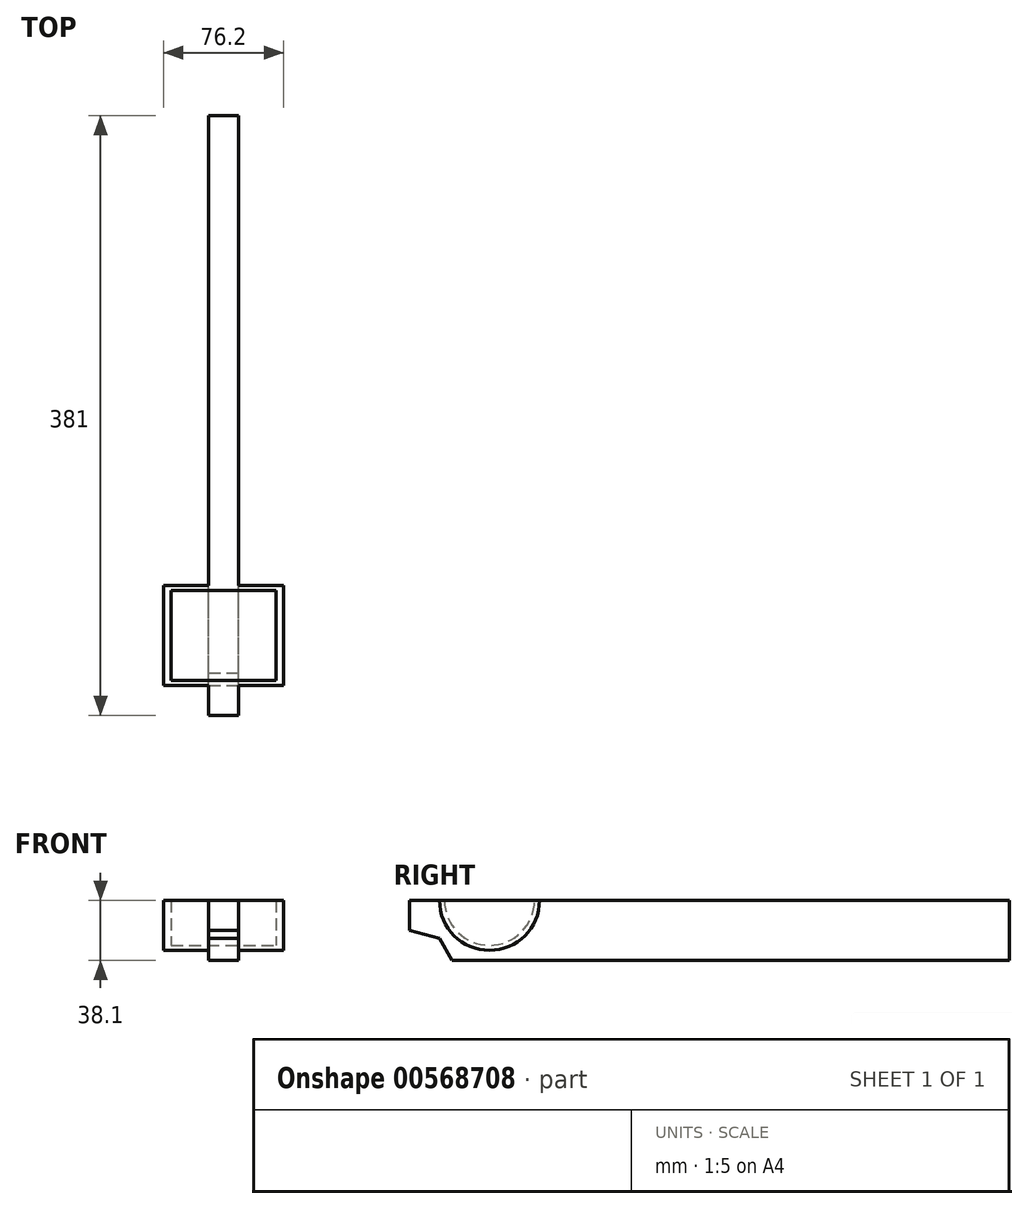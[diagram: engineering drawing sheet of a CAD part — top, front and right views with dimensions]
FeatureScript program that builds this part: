
annotation { "Feature Type Name" : "Feature", "Feature Type Description" : "" }
export const myFeature = defineFeature(function(context is Context, id is Id, definition is map)
    precondition{}
    {
        {
            var Q0;
            Q0=qCreatedBy(makeId("Front.planeOp"),FACE);
            var sketch = newSketch(context, id + "F0", { "sketchPlane" : qUnion([Q0])});
            skLineSegment(sketch, "E0.bottom", {"start": v(9.52, 19.05) * mm, "end": v(-9.53, 19.05) * mm});
            skLineSegment(sketch, "E0.top", {"start": v(9.52, -19.05) * mm, "end": v(-9.52, -19.05) * mm});
            skLineSegment(sketch, "E0.left", {"start": v(9.53, 19.05) * mm, "end": v(9.52, -19.05) * mm});
            skLineSegment(sketch, "E0.right", {"start": v(-9.53, 19.05) * mm, "end": v(-9.53, -19.05) * mm});
            skPoint(sketch, "E0.middle", {"position": v(0, 0) * mm});
            skSolve(sketch);
        }
        {
            var Q0;
            Q0 = qSketchRegion(id + "F0", true);
            extrude(context, id + "F1", {"entities" : qUnion([Q0]), "endBound" : BoundingType.SYMMETRIC, "depth" : 381 * mm, "offsetDistance" : 25.4 * mm});
        }
        {
            var Q0;
            Q0=qCreatedBy(makeId("Right.planeOp"),FACE);
            var sketch = newSketch(context, id + "F2", { "sketchPlane" : qUnion([Q0])});
            skLineSegment(sketch, "E1.1", {"start": v(-190.5, 19.05) * mm, "end": v(-190.5, -19.05) * mm, "construction": true});
            skLineSegment(sketch, "E1.2", {"start": v(-190.5, -19.05) * mm, "end": v(190.5, -19.05) * mm, "construction": true});
            skArc(sketch, "E2", {"start": v(-171.45, 19.05) * mm, "mid": v(-139.7, -12.7) * mm, "end": v(-107.95, 19.05) * mm});
            skLineSegment(sketch, "E3.0", {"start": v(-171.45, 19.05) * mm, "end": v(-107.95, 19.05) * mm});
            skPoint(sketch, "E4.orphan", {"position": v(190.5, 19.05) * mm});
            skSolve(sketch);
        }
        {
            var Q0;
            Q0 = qSketchRegion(id + "F2", true);
            extrude(context, id + "F3", {"entities" : qUnion([Q0]), "operationType" : NewBodyOperationType.ADD, "endBound" : BoundingType.SYMMETRIC, "depth" : 76.2 * mm, "offsetDistance" : 25.4 * mm});
        }
        {
            var Q0;
            Q0=makeQuery(id+"F3.boolean.opBoolean","MERGE",FACE,{"derivedFrom":[makeQuery(id+"F1.opExtrude","SWEPT_FACE",FACE,{"disambiguationData":[OSD([sQuery(id+"F0.wireOp",EDGE,"E0.bottom")])]}),makeQuery(id+"F3.opExtrude","SWEPT_FACE",FACE,{"disambiguationData":[OSD([sQuery(id+"F2.wireOp",EDGE,"E3.0")])]})]});
            var sketch = newSketch(context, id + "F4", { "sketchPlane" : qUnion([Q0])});
            skLineSegment(sketch, "E5", {"start": v(-9.52, -107.95) * mm, "end": v(9.53, -107.95) * mm, "construction": true});
            skLineSegment(sketch, "E6.1", {"start": v(-38.1, -171.45) * mm, "end": v(-38.1, -107.95) * mm, "construction": true});
            skLineSegment(sketch, "E6.2", {"start": v(-9.52, -107.95) * mm, "end": v(-38.1, -107.95) * mm, "construction": true});
            skLineSegment(sketch, "E6.3", {"start": v(38.1, -107.95) * mm, "end": v(9.53, -107.95) * mm, "construction": true});
            skLineSegment(sketch, "E6.4", {"start": v(38.1, -171.45) * mm, "end": v(38.1, -107.95) * mm, "construction": true});
            skLineSegment(sketch, "E7", {"start": v(-33.34, -168.28) * mm, "end": v(-33.34, -111.13) * mm});
            skLineSegment(sketch, "E8", {"start": v(-33.34, -111.13) * mm, "end": v(33.34, -111.13) * mm});
            skLineSegment(sketch, "E9", {"start": v(33.34, -111.12) * mm, "end": v(33.34, -168.28) * mm});
            skLineSegment(sketch, "E10", {"start": v(33.34, -168.28) * mm, "end": v(-33.34, -168.28) * mm});
            skLineSegment(sketch, "E11", {"start": v(-38.1, -171.45) * mm, "end": v(38.1, -171.45) * mm, "construction": true});
            skSolve(sketch);
        }
        {
            var Q0;
            Q0=makeQuery(id+"F3.opExtrude","CAP_FACE",FACE,{"disambiguationData":[OSD([sQuery(id+"F2.wireOp",EDGE,"E2"),sQuery(id+"F2.wireOp",EDGE,"E3.0")])],"isStart":false});
            var sketch = newSketch(context, id + "F5", { "sketchPlane" : qUnion([Q0])});
            skArc(sketch, "E12.0", {"start": v(-171.45, 19.05) * mm, "mid": v(-139.7, -12.7) * mm, "end": v(-107.95, 19.05) * mm, "construction": true});
            skLineSegment(sketch, "E13", {"start": v(-166.69, 19.05) * mm, "end": v(-112.71, 19.05) * mm});
            skArc(sketch, "E14.0", {"start": v(-166.69, 19.05) * mm, "mid": v(-139.7, -7.94) * mm, "end": v(-112.71, 19.05) * mm});
            skSolve(sketch);
        }
        {
            var Q0;
            Q0=makeQuery(id+"F4.imprint","IMPRINT",FACE,{"disambiguationData":[TD([[makeQuery(id+"F4.imprint","IMPRINT",EDGE,{"derivedFrom":sQuery(id+"F4.wireOp",EDGE,"E7")}),-1.0]])]});
            var sketch = newSketch(context, id + "F6", { "sketchPlane" : qUnion([Q0])});
            skLineSegment(sketch, "E15", {"start": v(38.1, -139.7) * mm, "end": v(78.66, -139.7) * mm, "construction": true});
            skLineSegment(sketch, "E16.bottom", {"start": v(33.34, -111.12) * mm, "end": v(-33.34, -111.12) * mm});
            skLineSegment(sketch, "E16.top", {"start": v(33.34, -139.7) * mm, "end": v(-33.34, -139.7) * mm});
            skLineSegment(sketch, "E16.left", {"start": v(33.34, -111.12) * mm, "end": v(33.34, -139.7) * mm});
            skLineSegment(sketch, "E16.right", {"start": v(-33.34, -111.13) * mm, "end": v(-33.34, -139.7) * mm});
            skSolve(sketch);
        }
        {
            var Q0;
            Q0 = qSketchRegion(id + "F6", true);
            var Q1;
            Q1=sQuery(id+"F6.wireOp",EDGE,"E15");
            revolve(context, id + "F7", {"operationType" : NewBodyOperationType.REMOVE, "entities" : qUnion([Q0]), "axis" : qUnion([Q1]), "revolveType" : RevolveType.FULL, "oppositeDirection" : true});
        }
        {
            var Q0;
            Q0=makeQuery(id+"F1.opExtrude","SWEPT_FACE",FACE,{"disambiguationData":[OSD([sQuery(id+"F0.wireOp",EDGE,"E0.left")])]});
            var sketch = newSketch(context, id + "F8", { "sketchPlane" : qUnion([Q0])});
            skLineSegment(sketch, "E17.0", {"start": v(-190.5, 0) * mm, "end": v(-190.5, -19.05) * mm});
            skLineSegment(sketch, "E17.1", {"start": v(-190.5, -19.05) * mm, "end": v(-163.45, -19.05) * mm});
            skLineSegment(sketch, "E18", {"start": v(-190.5, 0) * mm, "end": v(-171.45, -5.2) * mm});
            skLineSegment(sketch, "E19", {"start": v(-171.45, -5.2) * mm, "end": v(-163.45, -19.05) * mm});
            skPoint(sketch, "E20.orphan", {"position": v(190.5, -19.05) * mm});
            skPoint(sketch, "E21.orphan", {"position": v(-190.5, 19.05) * mm});
            skSolve(sketch);
        }
        {
            var Q0;
            Q0 = qSketchRegion(id + "F8", true);
            extrude(context, id + "F9", {"entities" : qUnion([Q0]), "operationType" : NewBodyOperationType.REMOVE, "endBound" : BoundingType.THROUGH_ALL, "oppositeDirection" : true, "depth" : 25.4 * mm, "offsetDistance" : 25.4 * mm});
        }
    });
